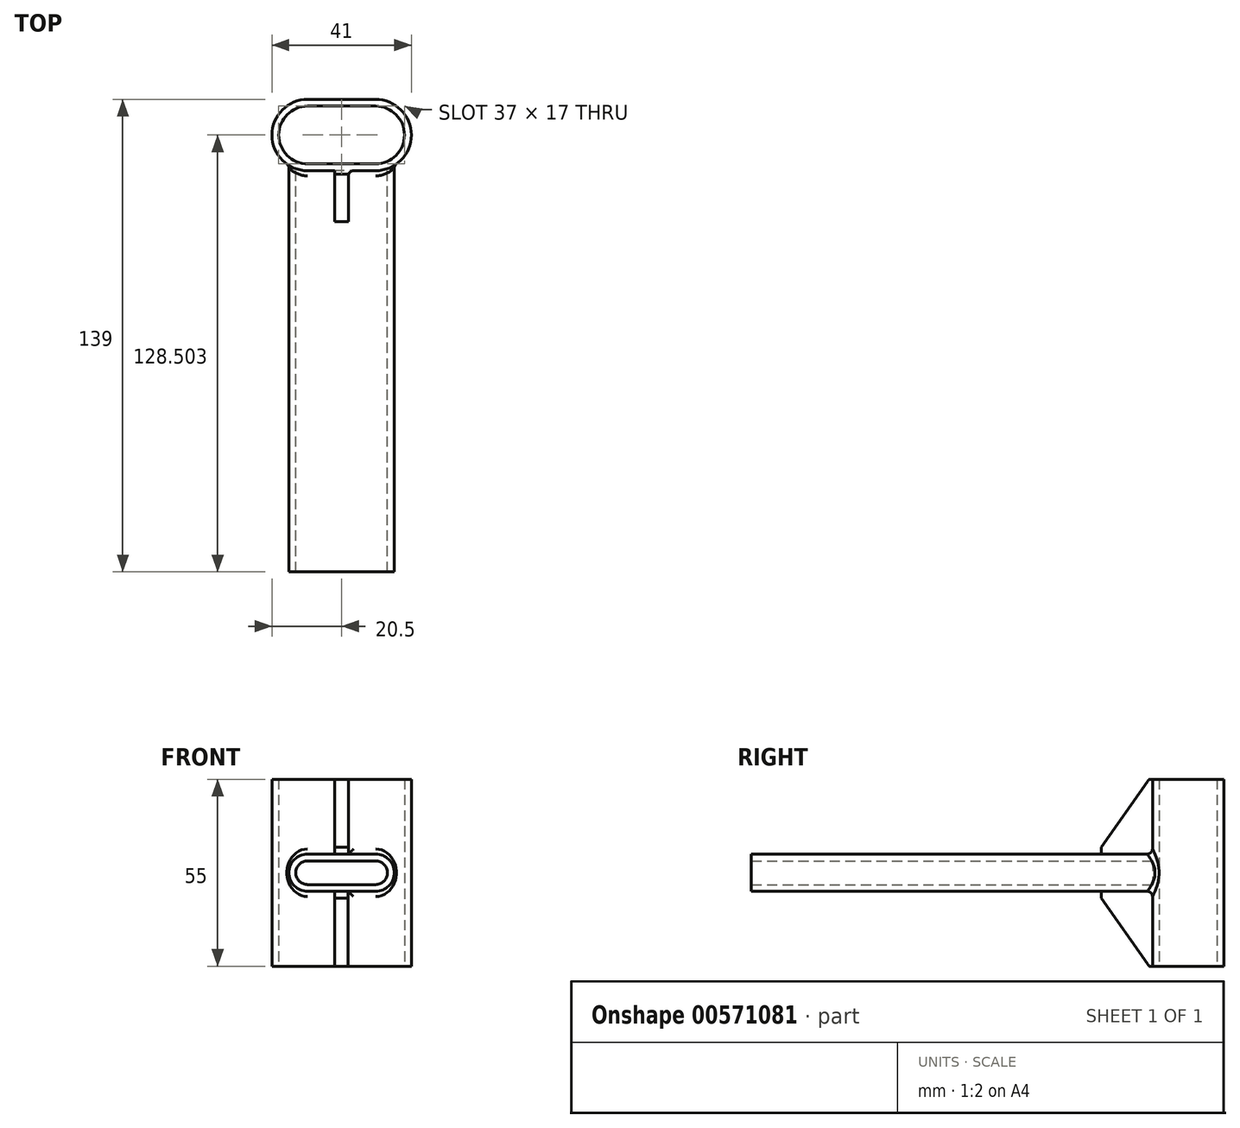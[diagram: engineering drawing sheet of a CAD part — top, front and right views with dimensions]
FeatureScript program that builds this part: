
annotation { "Feature Type Name" : "Feature", "Feature Type Description" : "" }
export const myFeature = defineFeature(function(context is Context, id is Id, definition is map)
    precondition{}
    {
        {
            var Q0;
            Q0=qCreatedBy(makeId("Top.planeOp"),FACE);
            var sketch = newSketch(context, id + "F0", { "sketchPlane" : qUnion([Q0])});
            skLineSegment(sketch, "E0", {"start": v(0, -15.99) * mm, "end": v(-10, -15.99) * mm});
            skArc(sketch, "E1", {"start": v(-10, 5.01) * mm, "mid": v(-20.5, -5.49) * mm, "end": v(-10, -15.99) * mm});
            skLineSegment(sketch, "E2", {"start": v(-10, 5.01) * mm, "end": v(0, 5.01) * mm});
            skLineSegment(sketch, "E3.MirrorCS", {"start": v(0, -15.99) * mm, "end": v(10, -15.99) * mm});
            skLineSegment(sketch, "E4.MirrorCS", {"start": v(10, 5.01) * mm, "end": v(0, 5.01) * mm});
            skArc(sketch, "E5.MirrorCS", {"start": v(10, 5.01) * mm, "mid": v(20.5, -5.49) * mm, "end": v(10, -15.99) * mm});
            skLineSegment(sketch, "E6.0", {"start": v(10, 3.01) * mm, "end": v(0, 3.01) * mm});
            skLineSegment(sketch, "E6.1", {"start": v(0, -13.99) * mm, "end": v(10, -13.99) * mm});
            skLineSegment(sketch, "E6.2", {"start": v(0, -13.99) * mm, "end": v(-10, -13.99) * mm});
            skArc(sketch, "E6.3", {"start": v(10, 3.01) * mm, "mid": v(18.5, -5.49) * mm, "end": v(10, -13.99) * mm});
            skArc(sketch, "E6.4", {"start": v(-10, 3.01) * mm, "mid": v(-18.5, -5.49) * mm, "end": v(-10, -13.99) * mm});
            skLineSegment(sketch, "E6.5", {"start": v(-10, 3.01) * mm, "end": v(0, 3.01) * mm});
            skSolve(sketch);
        }
        {
            var Q0;
            Q0=makeQuery(id+"F0.imprint","IMPRINT",FACE,{"disambiguationData":[TD([[makeQuery(id+"F0.imprint","IMPRINT",EDGE,{"derivedFrom":sQuery(id+"F0.wireOp",EDGE,"E0")}),-1.0]])]});
            extrude(context, id + "F1", {"entities" : qUnion([Q0]), "endBound" : BoundingType.SYMMETRIC, "depth" : 55 * mm, "offsetDistance" : 25 * mm});
        }
        {
            var Q0;
            Q0=makeQuery(id+"F1.opExtrude","SWEPT_FACE",FACE,{"disambiguationData":[OSD([sQuery(id+"F0.wireOp",EDGE,"E6.1"),sQuery(id+"F0.wireOp",EDGE,"E6.2")])]});
            var sketch = newSketch(context, id + "F2", { "sketchPlane" : qUnion([Q0])});
            skLineSegment(sketch, "E7.bottom", {"start": v(10, -5.5) * mm, "end": v(-10, -5.5) * mm});
            skLineSegment(sketch, "E7.top", {"start": v(10, 5.5) * mm, "end": v(-10, 5.5) * mm});
            skLineSegment(sketch, "E7.left", {"start": v(15.5, 0) * mm, "end": v(15.5, 0) * mm});
            skLineSegment(sketch, "E7.right", {"start": v(-15.5, 0) * mm, "end": v(-15.5, 0) * mm});
            skPoint(sketch, "E7.middle", {"position": v(0, 0) * mm});
            skPoint(sketch, "E8.visualSharp", {"position": v(-15.5, 5.5) * mm});
            skArc(sketch, "E8.filletArc", {"start": v(-10, 5.5) * mm, "mid": v(-13.89, 3.89) * mm, "end": v(-15.5, 0) * mm});
            skPoint(sketch, "E9.visualSharp", {"position": v(15.5, 5.5) * mm});
            skArc(sketch, "E9.filletArc", {"start": v(15.5, 0) * mm, "mid": v(13.89, 3.89) * mm, "end": v(10, 5.5) * mm});
            skPoint(sketch, "E10.visualSharp", {"position": v(15.5, -5.5) * mm});
            skArc(sketch, "E10.filletArc", {"start": v(10, -5.5) * mm, "mid": v(13.89, -3.89) * mm, "end": v(15.5, 0) * mm});
            skPoint(sketch, "E11.visualSharp", {"position": v(-15.5, -5.5) * mm});
            skArc(sketch, "E11.filletArc", {"start": v(-15.5, 0) * mm, "mid": v(-13.89, -3.89) * mm, "end": v(-10, -5.5) * mm});
            skArc(sketch, "E12.0", {"start": v(10, -3.5) * mm, "mid": v(12.47, -2.47) * mm, "end": v(13.5, 0) * mm});
            skArc(sketch, "E12.1", {"start": v(-13.5, 0) * mm, "mid": v(-12.47, -2.47) * mm, "end": v(-10, -3.5) * mm});
            skArc(sketch, "E12.2", {"start": v(-10, 3.5) * mm, "mid": v(-12.47, 2.47) * mm, "end": v(-13.5, 0) * mm});
            skLineSegment(sketch, "E12.3", {"start": v(10, -3.5) * mm, "end": v(-10, -3.5) * mm});
            skLineSegment(sketch, "E12.4", {"start": v(10, 3.5) * mm, "end": v(-10, 3.5) * mm});
            skArc(sketch, "E12.5", {"start": v(13.5, 0) * mm, "mid": v(12.47, 2.47) * mm, "end": v(10, 3.5) * mm});
            skSolve(sketch);
        }
        {
            var Q0;
            {var subQ0=sQuery(id+"F2.wireOp",EDGE,"E7.bottom");Q0=makeQuery(id+"F2.imprint","IMPRINT",FACE,{"disambiguationData":[TD([[makeQuery(id+"F2.imprint","IMPRINT",EDGE,{"derivedFrom":subQ0}),-1.0]])]});}
            var Q1;
            {var subQ0=sQuery(id+"F2.wireOp",EDGE,"E8.filletArc");Q1=makeQuery(id+"F2.imprint","IMPRINT",FACE,{"disambiguationData":[TD([[makeQuery(id+"F2.imprint","IMPRINT",EDGE,{"derivedFrom":subQ0}),1.0]])]});}
            var Q2;
            {var subQ0=sQuery(id+"F2.wireOp",EDGE,"E9.filletArc");Q2=makeQuery(id+"F2.imprint","IMPRINT",FACE,{"disambiguationData":[TD([[makeQuery(id+"F2.imprint","IMPRINT",EDGE,{"derivedFrom":subQ0}),1.0]])]});}
            var Q3;
            {var subQ0=sQuery(id+"F2.wireOp",EDGE,"E7.top");Q3=makeQuery(id+"F2.imprint","IMPRINT",FACE,{"disambiguationData":[TD([[makeQuery(id+"F2.imprint","IMPRINT",EDGE,{"derivedFrom":subQ0}),1.0]])]});}
            extrude(context, id + "F3", {"entities" : qUnion([Q0, Q1, Q2, Q3]), "operationType" : NewBodyOperationType.ADD, "oppositeDirection" : true, "depth" : 120 * mm, "offsetDistance" : 25 * mm});
        }
        {
            var Q0;
            {var subQ2=sQuery(id+"F0.wireOp",EDGE,"E3.MirrorCS");var subQ3=sQuery(id+"F0.wireOp",EDGE,"E0");Q0=makeQuery(id+"F3.boolean.opBoolean","SPLIT",FACE,{"disambiguationData":[TD([makeQuery(id+"F3.opExtrude","SWEPT_FACE",FACE,{"disambiguationData":[OSD([sQuery(id+"F2.wireOp",EDGE,"E7.top")])]})])],"derivedFrom":makeQuery(id+"F1.opExtrude","SWEPT_FACE",FACE,{"disambiguationData":[OSD([subQ3,subQ2])]})});}
            var sketch = newSketch(context, id + "F4", { "sketchPlane" : qUnion([Q0])});
            skLineSegment(sketch, "E13.right", {"start": v(2, 27.5) * mm, "end": v(2, 5.5) * mm});
            skLineSegment(sketch, "E14", {"start": v(0, 27.5) * mm, "end": v(0, 5.5) * mm, "construction": true});
            skLineSegment(sketch, "E15.MirrorCS", {"start": v(-2, 27.5) * mm, "end": v(-2, 5.5) * mm});
            skLineSegment(sketch, "E16", {"start": v(2, 27.5) * mm, "end": v(-2, 27.5) * mm});
            skLineSegment(sketch, "E17", {"start": v(-2, 5.5) * mm, "end": v(2, 5.5) * mm});
            skSolve(sketch);
        }
        {
            var Q0;
            Q0=makeQuery(id+"F4.imprint","IMPRINT",FACE,{"disambiguationData":[TD([[makeQuery(id+"F4.imprint","IMPRINT",EDGE,{"derivedFrom":sQuery(id+"F4.wireOp",EDGE,"E13.right")}),-1.0]])]});
            extrude(context, id + "F5", {"entities" : qUnion([Q0]), "operationType" : NewBodyOperationType.ADD, "depth" : 15 * mm, "offsetDistance" : 25 * mm});
        }
        {
            var Q0;
            Q0=makeQuery(id+"F5.opExtrude","CAP_EDGE",EDGE,{"disambiguationData":[OSD([sQuery(id+"F4.wireOp",EDGE,"E16")])],"isStart":false});
            chamfer(context, id + "F6", {"entities" : qUnion([Q0]), "chamferType" : ChamferType.OFFSET_ANGLE, "width" : 20 * mm, "oppositeDirection" : false, "angle" : 35 * degree, "tangentPropagation" : true});
        }
        {
            var Q0;
            {var subQ2=sQuery(id+"F0.wireOp",EDGE,"E3.MirrorCS");var subQ3=sQuery(id+"F0.wireOp",EDGE,"E0");Q0=makeQuery(id+"F3.boolean.opBoolean","SPLIT",FACE,{"disambiguationData":[TD([makeQuery(id+"F3.opExtrude","SWEPT_FACE",FACE,{"disambiguationData":[OSD([sQuery(id+"F2.wireOp",EDGE,"E7.bottom")])]})])],"derivedFrom":makeQuery(id+"F1.opExtrude","SWEPT_FACE",FACE,{"disambiguationData":[OSD([subQ3,subQ2])]})});}
            var sketch = newSketch(context, id + "F7", { "sketchPlane" : qUnion([Q0])});
            skLineSegment(sketch, "E18.bottom", {"start": v(0, -5.5) * mm, "end": v(1.92, -5.5) * mm});
            skLineSegment(sketch, "E19.MirrorCS", {"start": v(0, -5.5) * mm, "end": v(-2.08, -5.5) * mm});
            skLineSegment(sketch, "E20.right", {"start": v(1.92, -5.5) * mm, "end": v(1.92, -27.5) * mm});
            skLineSegment(sketch, "E21", {"start": v(-0.08, -5.5) * mm, "end": v(-0.08, -27.5) * mm, "construction": true});
            skLineSegment(sketch, "E22.MirrorCS", {"start": v(-2.08, -5.5) * mm, "end": v(-2.08, -27.5) * mm});
            skLineSegment(sketch, "E23", {"start": v(1.92, -5.5) * mm, "end": v(-2.08, -5.5) * mm});
            skPoint(sketch, "E24.orphan", {"position": v(3, -5.5) * mm});
            skPoint(sketch, "E25.MirrorCS.start.orphan", {"position": v(-3, -5.5) * mm});
            skLineSegment(sketch, "E26", {"start": v(-2.08, -27.5) * mm, "end": v(1.92, -27.5) * mm});
            skSolve(sketch);
        }
        {
            var Q0;
            Q0=makeQuery(id+"F7.imprint","IMPRINT",FACE,{"disambiguationData":[TD([[makeQuery(id+"F7.imprint","IMPRINT",EDGE,{"derivedFrom":sQuery(id+"F7.wireOp",EDGE,"E20.right")}),-1.0]])]});
            extrude(context, id + "F8", {"entities" : qUnion([Q0]), "operationType" : NewBodyOperationType.ADD, "depth" : 15 * mm, "offsetDistance" : 25 * mm});
        }
        {
            var Q0;
            Q0=makeQuery(id+"F8.opExtrude","CAP_EDGE",EDGE,{"disambiguationData":[OSD([sQuery(id+"F7.wireOp",EDGE,"E18.top"),sQuery(id+"F7.wireOp",EDGE,"f78b57d4-ba43-493b-bf49-fca4234a849f.MirrorCS")])],"isStart":false});
            var Q1;
            Q1=makeQuery(id+"F8.opExtrude","CAP_EDGE",EDGE,{"disambiguationData":[OSD([sQuery(id+"F7.wireOp",EDGE,"E26")])],"isStart":false});
            chamfer(context, id + "F9", {"entities" : qUnion([Q0, Q1]), "chamferType" : ChamferType.OFFSET_ANGLE, "width" : 20 * mm, "oppositeDirection" : true, "angle" : 35 * degree, "tangentPropagation" : true});
        }
        {
            var Q0;
            Q0=makeQuery(id+"F5.opExtrude","CAP_EDGE",EDGE,{"disambiguationData":[OSD([sQuery(id+"F4.wireOp",EDGE,"E15.MirrorCS")])],"isStart":true});
            var Q1;
            Q1=makeQuery(id+"F5.opExtrude","SWEPT_EDGE",EDGE,{"disambiguationData":[OSD([sQuery(id+"F0.wireOp",EDGE,"E0"),sQuery(id+"F0.wireOp",EDGE,"E3.MirrorCS"),sQuery(id+"F2.wireOp",EDGE,"E7.top"),sQuery(id+"F4.wireOp",EDGE,"E15.MirrorCS"),sQuery(id+"F4.wireOp",EDGE,"E17")])]});
            var Q2;
            Q2=makeQuery(id+"F5.opExtrude","CAP_EDGE",EDGE,{"disambiguationData":[OSD([sQuery(id+"F4.wireOp",EDGE,"E17")])],"isStart":false});
            var Q3;
            Q3=makeQuery(id+"F5.opExtrude","SWEPT_EDGE",EDGE,{"disambiguationData":[OSD([sQuery(id+"F0.wireOp",EDGE,"E0"),sQuery(id+"F0.wireOp",EDGE,"E3.MirrorCS"),sQuery(id+"F2.wireOp",EDGE,"E7.top"),sQuery(id+"F4.wireOp",EDGE,"E13.right"),sQuery(id+"F4.wireOp",EDGE,"E17")])]});
            var Q4;
            Q4=makeQuery(id+"F5.opExtrude","CAP_EDGE",EDGE,{"disambiguationData":[OSD([sQuery(id+"F4.wireOp",EDGE,"E13.right")])],"isStart":true});
            var Q5;
            {var subQ0=makeQuery(id+"F3.opExtrude","SWEPT_FACE",FACE,{"disambiguationData":[OSD([sQuery(id+"F2.wireOp",EDGE,"E7.top")])]});var subQ1=makeQuery(id+"F1.opExtrude","SWEPT_FACE",FACE,{"disambiguationData":[OSD([sQuery(id+"F0.wireOp",EDGE,"E0"),sQuery(id+"F0.wireOp",EDGE,"E3.MirrorCS")])]});Q5=makeQuery(id+"F5.boolean.opBoolean","SPLIT",EDGE,{"disambiguationData":[TD([makeQuery(id+"F1.opExtrude","SWEPT_FACE",FACE,{"disambiguationData":[OSD([sQuery(id+"F0.wireOp",EDGE,"E5.MirrorCS")])]})])],"derivedFrom":makeQuery(id+"F3.boolean.opBoolean","INTERSECT",EDGE,{"derivedFrom":[subQ1,subQ0]})});}
            var Q6;
            {var subQ0=makeQuery(id+"F3.opExtrude","SWEPT_FACE",FACE,{"disambiguationData":[OSD([sQuery(id+"F2.wireOp",EDGE,"E7.top")])]});var subQ1=makeQuery(id+"F1.opExtrude","SWEPT_FACE",FACE,{"disambiguationData":[OSD([sQuery(id+"F0.wireOp",EDGE,"E0"),sQuery(id+"F0.wireOp",EDGE,"E3.MirrorCS")])]});Q6=makeQuery(id+"F5.boolean.opBoolean","SPLIT",EDGE,{"disambiguationData":[TD([makeQuery(id+"F1.opExtrude","SWEPT_FACE",FACE,{"disambiguationData":[OSD([sQuery(id+"F0.wireOp",EDGE,"E1")])]})])],"derivedFrom":makeQuery(id+"F3.boolean.opBoolean","INTERSECT",EDGE,{"derivedFrom":[subQ1,subQ0]})});}
            var Q7;
            Q7=makeQuery(id+"F8.opExtrude","CAP_EDGE",EDGE,{"disambiguationData":[OSD([sQuery(id+"F7.wireOp",EDGE,"E22.MirrorCS")])],"isStart":true});
            var Q8;
            Q8=makeQuery(id+"F8.opExtrude","SWEPT_EDGE",EDGE,{"disambiguationData":[OSD([sQuery(id+"F0.wireOp",EDGE,"E0"),sQuery(id+"F0.wireOp",EDGE,"E3.MirrorCS"),sQuery(id+"F2.wireOp",EDGE,"E7.bottom"),sQuery(id+"F7.wireOp",EDGE,"E22.MirrorCS"),sQuery(id+"F7.wireOp",EDGE,"E23")])]});
            var Q9;
            Q9=makeQuery(id+"F8.opExtrude","CAP_EDGE",EDGE,{"disambiguationData":[OSD([sQuery(id+"F7.wireOp",EDGE,"E20.right")])],"isStart":true});
            var Q10;
            Q10=makeQuery(id+"F8.opExtrude","SWEPT_EDGE",EDGE,{"disambiguationData":[OSD([sQuery(id+"F0.wireOp",EDGE,"E0"),sQuery(id+"F0.wireOp",EDGE,"E3.MirrorCS"),sQuery(id+"F2.wireOp",EDGE,"E7.bottom"),sQuery(id+"F7.wireOp",EDGE,"E20.right"),sQuery(id+"F7.wireOp",EDGE,"E23")])]});
            var Q11;
            Q11=makeQuery(id+"F8.opExtrude","CAP_EDGE",EDGE,{"disambiguationData":[OSD([sQuery(id+"F7.wireOp",EDGE,"E23")])],"isStart":false});
            fillet(context, id + "F10", {"entities" : qUnion([Q0, Q1, Q2, Q3, Q4, Q5, Q6, Q7, Q8, Q9, Q10, Q11]), "radius" : 1.5 * mm, "tangentPropagation" : true, "allowEdgeOverflow" : false});
        }
    });
